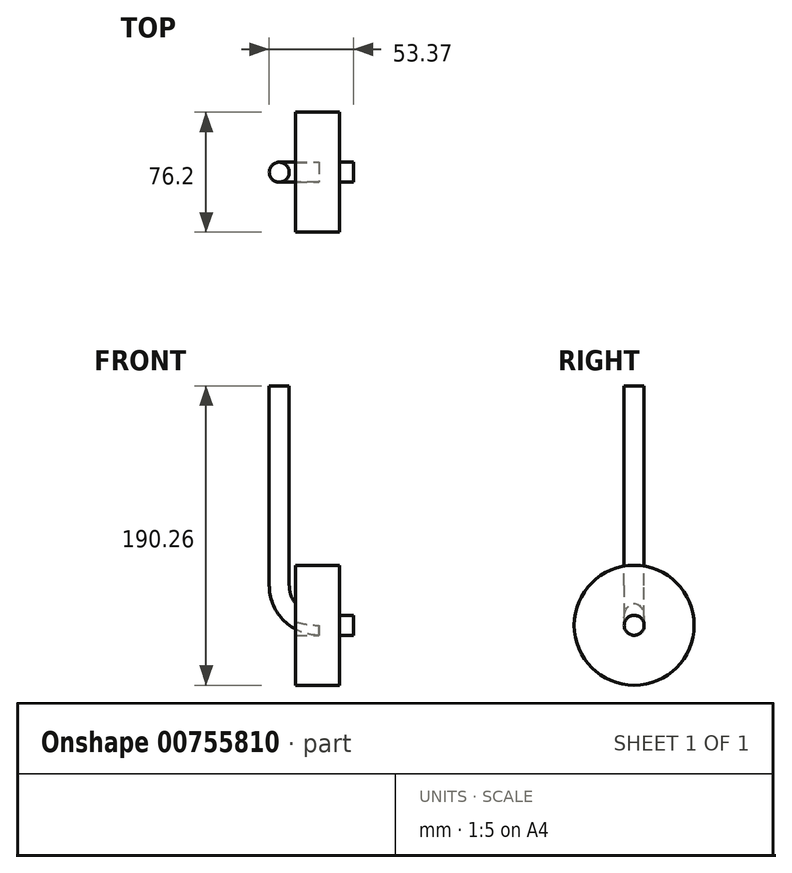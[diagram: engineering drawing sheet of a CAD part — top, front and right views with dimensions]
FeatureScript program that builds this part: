
annotation { "Feature Type Name" : "Feature", "Feature Type Description" : "" }
export const myFeature = defineFeature(function(context is Context, id is Id, definition is map)
    precondition{}
    {
        {
            var Q0;
            Q0=qCreatedBy(makeId("Top.planeOp"),FACE);
            var sketch = newSketch(context, id + "F0", { "sketchPlane" : qUnion([Q0])});
            skCircle(sketch, "E0", {"center": v(0, 0) * mm, "radius": 6.35 * mm});
            skSolve(sketch);
        }
        {
            var Q0;
            Q0=qSketchRegion(id+"F0",true);
            extrude(context, id + "F1", {"entities" : qUnion([Q0]), "oppositeDirection" : true, "depth" : 101.6 * mm, "offsetDistance" : 25.4 * mm});
        }
        {
            var Q0;
            Q0=qCreatedBy(makeId("Front.planeOp"),FACE);
            var sketch = newSketch(context, id + "F2", { "sketchPlane" : qUnion([Q0])});
            skLineSegment(sketch, "E1.top", {"start": v(25.4, -152.16) * mm, "end": v(38.38, -152.16) * mm});
            skLineSegment(sketch, "E1.left", {"start": v(0, -100.06) * mm, "end": v(0, -126.76) * mm});
            skPoint(sketch, "E2.visualSharp", {"position": v(0, -152.16) * mm});
            skArc(sketch, "E2.filletArc", {"start": v(0, -126.76) * mm, "mid": v(7.44, -144.72) * mm, "end": v(25.4, -152.16) * mm});
            skSolve(sketch);
        }
        {
            var Q0;
            Q0=makeQuery(id+"F1.opExtrude","CAP_FACE",FACE,{"disambiguationData":[OSD([sQuery(id+"F0.wireOp",EDGE,"E0")])],"isStart":false});
            var Q1;
            Q1=sQuery(id+"F2.wireOp",EDGE,"E1.left");
            var Q2;
            Q2=sQuery(id+"F2.wireOp",EDGE,"E2.filletArc");
            var Q3;
            Q3=sQuery(id+"F2.wireOp",EDGE,"E1.top");
            sweep(context, id + "F3", {"operationType" : NewBodyOperationType.ADD, "profiles" : qUnion([Q0]), "path" : qUnion([Q1, Q2, Q3])});
        }
        {
            var Q0;
            Q0=makeQuery(id+"F3.opSweep","CAP_FACE",FACE,{"disambiguationData":[OSD([sQuery(id+"F0.wireOp",EDGE,"E0"),sQuery(id+"F2.wireOp",VERTEX,"E1.top.end")])],"isStart":false});
            var sketch = newSketch(context, id + "F4", { "sketchPlane" : qUnion([Q0])});
            skCircle(sketch, "E3", {"center": v(0, -152.16) * mm, "radius": 6.35 * mm});
            skCircle(sketch, "E4", {"center": v(0, -152.16) * mm, "radius": 38.1 * mm});
            skSolve(sketch);
        }
        {
            var Q0;
            Q0=makeQuery(id+"F4.imprint","IMPRINT",FACE,{"disambiguationData":[TD([[makeQuery(id+"F4.imprint","IMPRINT",EDGE,{"derivedFrom":sQuery(id+"F4.wireOp",EDGE,"E3")}),-1.0]])]});
            extrude(context, id + "F5", {"entities" : qUnion([Q0]), "oppositeDirection" : true, "depth" : 28.2 * mm, "offsetDistance" : 25.4 * mm});
        }
        {
            var Q0;
            Q0=makeQuery(id+"F5.boolean.opBoolean","MERGE",FACE,{"derivedFrom":[makeQuery(id+"F3.opSweep","CAP_FACE",FACE,{"disambiguationData":[OSD([sQuery(id+"F0.wireOp",EDGE,"E0"),sQuery(id+"F2.wireOp",VERTEX,"E1.top.end")])],"isStart":false}),makeQuery(id+"F5.opExtrude","CAP_FACE",FACE,{"disambiguationData":[OSD([sQuery(id+"F4.wireOp",EDGE,"E3"),sQuery(id+"F4.wireOp",EDGE,"E4")])],"isStart":true})]});
            var sketch = newSketch(context, id + "F6", { "sketchPlane" : qUnion([Q0])});
            skCircle(sketch, "E5", {"center": v(0, -152.16) * mm, "radius": 6.35 * mm});
            skSolve(sketch);
        }
        {
            var Q0;
            Q0=qSketchRegion(id+"F6",true);
            extrude(context, id + "F7", {"entities" : qUnion([Q0]), "operationType" : NewBodyOperationType.ADD, "depth" : 8.64 * mm, "offsetDistance" : 25.4 * mm});
        }
    });
